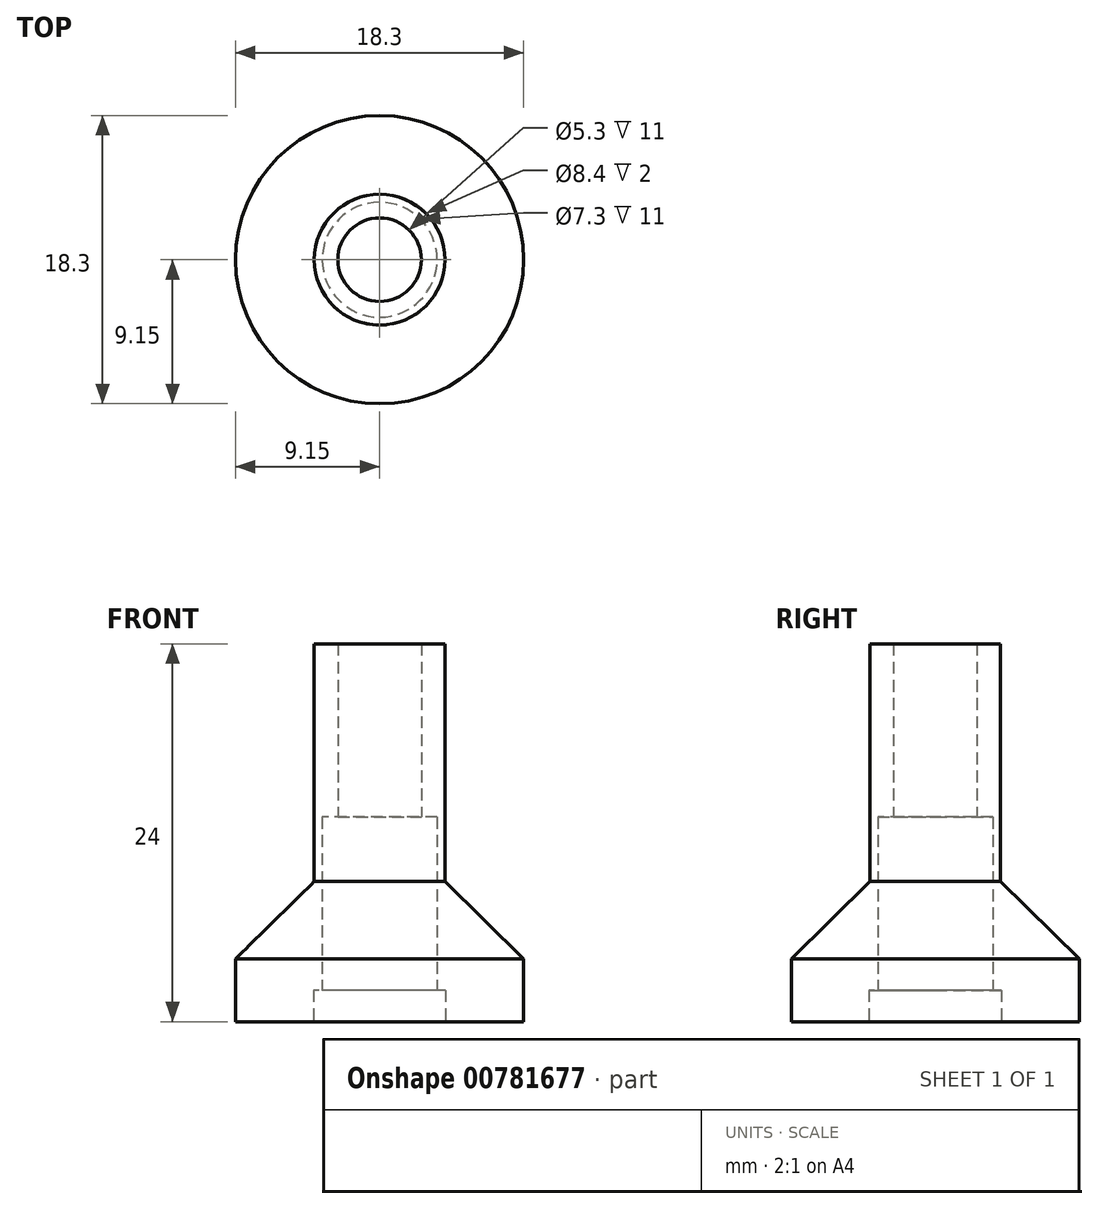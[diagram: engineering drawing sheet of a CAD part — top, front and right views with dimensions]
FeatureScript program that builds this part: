
annotation { "Feature Type Name" : "Feature", "Feature Type Description" : "" }
export const myFeature = defineFeature(function(context is Context, id is Id, definition is map)
    precondition{}
    {
        {
            var Q0;
            Q0=qCreatedBy(makeId("Front.planeOp"),FACE);
            var sketch = newSketch(context, id + "F0", { "sketchPlane" : qUnion([Q0])});
            skLineSegment(sketch, "E0", {"start": v(0, 0) * mm, "end": v(0, 26.75) * mm, "construction": true});
            skLineSegment(sketch, "E1.bottom", {"start": v(-2.65, 0) * mm, "end": v(-4.15, 0) * mm});
            skLineSegment(sketch, "E1.top", {"start": v(-2.65, 24) * mm, "end": v(-4.15, 24) * mm});
            skLineSegment(sketch, "E1.left", {"start": v(-2.65, 0) * mm, "end": v(-2.65, 24) * mm});
            skLineSegment(sketch, "E1.right", {"start": v(-4.15, 0) * mm, "end": v(-4.15, 24) * mm});
            skLineSegment(sketch, "E2.bottom", {"start": v(-4.15, 0) * mm, "end": v(-9.15, 0) * mm});
            skLineSegment(sketch, "E2.top", {"start": v(-4.15, 4) * mm, "end": v(-9.15, 4) * mm});
            skLineSegment(sketch, "E2.left", {"start": v(-4.15, 0) * mm, "end": v(-4.15, 4) * mm});
            skLineSegment(sketch, "E2.right", {"start": v(-9.15, 0) * mm, "end": v(-9.15, 4) * mm});
            skLineSegment(sketch, "E3", {"start": v(-9.15, 4) * mm, "end": v(-4.15, 8.9) * mm});
            skSolve(sketch);
        }
        {
            var Q0;
            Q0 = qSketchRegion(id + "F0", true);
            var Q1;
            Q1=sQuery(id+"F0.wireOp",EDGE,"E0");
            revolve(context, id + "F1", {"surfaceOperationType" : NewSurfaceOperationType.NEW, "entities" : qUnion([Q0]), "axis" : qUnion([Q1]), "revolveType" : RevolveType.FULL});
        }
        {
            var Q0;
            Q0=qCreatedBy(makeId("Top.planeOp"),FACE);
            var sketch = newSketch(context, id + "F2", { "sketchPlane" : qUnion([Q0])});
            skCircle(sketch, "E4", {"center": v(0, 0) * mm, "radius": 4.2 * mm});
            skCircle(sketch, "E5", {"center": v(0, 0) * mm, "radius": 3.65 * mm});
            skSolve(sketch);
        }
        {
            var Q0;
            Q0=makeQuery(id+"F2.imprint","IMPRINT",FACE,{"disambiguationData":[TD([[makeQuery(id+"F2.imprint","IMPRINT",EDGE,{"derivedFrom":sQuery(id+"F2.wireOp",EDGE,"E4")}),1.0]])]});
            extrude(context, id + "F3", {"entities" : qUnion([Q0]), "operationType" : NewBodyOperationType.REMOVE, "depth" : 2 * mm, "offsetDistance" : 25 * mm});
        }
        {
            var Q0;
            Q0=makeQuery(id+"F3.boolean.opBoolean","SPLIT",FACE,{"disambiguationData":[TD([makeQuery(id+"F1.opRevolve","SWEPT_FACE",FACE,{"disambiguationData":[OSD([sQuery(id+"F0.wireOp",EDGE,"E1.left")])]})])],"derivedFrom":makeQuery(id+"F1.opRevolve","SWEPT_FACE",FACE,{"disambiguationData":[OSD([sQuery(id+"F0.wireOp",EDGE,"E1.bottom"),sQuery(id+"F0.wireOp",EDGE,"E2.bottom")])]})});
            extrude(context, id + "F4", {"entities" : qUnion([Q0]), "operationType" : NewBodyOperationType.REMOVE, "oppositeDirection" : true, "depth" : 13 * mm, "offsetDistance" : 25 * mm});
        }
    });
